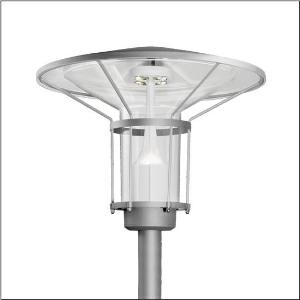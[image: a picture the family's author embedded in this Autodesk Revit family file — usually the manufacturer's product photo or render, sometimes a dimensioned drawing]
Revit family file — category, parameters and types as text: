
# Revit family: laterne_classic_iq___st1_2a_5xa5245af14h_9f1a
name_source: partatom
category: Lighting Fixtures
units: mm (PartAtom-declared; Revit-internal decimal feet)

## family parameters
Cut with Voids When Loaded = No
Host = Face
Light Source = No
Part Type = Normal
Room Calculation Point = No
Round Connector Dimension = Use Diameter
Shared = No

## types (1)
- --- (1 x LED, 1380 lm, 12.9 W, 2200K)
    Apparent Load = 13 VA
    CIE Flux Codes = 21 60 93 97 100
    Color Rendering = 70
    Color Temperature = 2200K
    Default Elevation = 1800 mm
    Description = Lantern Classic iQ, mast luminaire, Module 540 iQ-SR, primary light control with 3 zone facetted reflector, of plastic, silver coated, highly specular, structured, primary optical cover: cover, of PMMA, transparent, light distribution: ST1.2a, light emission: direct distribution, primary light characteristic: asymmetric, installation type: post-top, LED, High Power LED, rated luminous flux: 1.380lm, luminous efficacy: 107lm/W, light colour: 722, colour temperature: 2200K, control gear: ECG iQ, control: presetting dimming logarithmic, Street-Remote, Auto-Match, Temp-Guard, Lumen-Switch, Night-Set, Smart-Wire, Light-Fading, Desk-Remote (wireless, voltage-free reading and setting of iQ features in the workshop via application-optimized NFC function/RFID function), optimised constant luminous flux control (CLO 2.0), with terminal, 6-pole, max. 2.5mm², mains connection: 230..240V, AC, 50/60Hz, start of lifetime: 13W, end of service life: 13W, reduction: 6W, luminaire housing, upper part, of glass-fibre reinforced polyester, coated, Siteco® metallic grey (DB 702S), diameter: 750mm, height: 596mm, spigot size: d x l = 76 x 70mm (post-top) | with reducer (optional accessory) 60 x 70mm, post-top mast mounting element, of diecast aluminium, coated, Siteco® metallic grey (DB 702S), Module 540 iQ-SR, traffic white (RAL 9016), equipment: standard, protection rating (complete): IP65, insulation class (complete): insulation class II (safety insulation), certification: CE, ENEC, VDE, packaging unit: 1 piece

Light Distribution: ST1.2a
    Height = 596 mm
    Lamp = 1 x LED
    Lamp Light Flux = 1380 lm
    Lamp Power = 12.9 W
    Lamp count = 1
    Length = 750 mm
    Luminous efficacy = 107 lm/W
    Manufacturer = Siteco
    ModVariant = No
    Model = 5XA5245AF14H
    Number of Poles = 1
    OnlyDefault = Yes
    Power Factor = 1
    Product Name = Laterne Classic iQ | ST1.2a
    Product group = mast luminaire | pylon top
    ProductGroupID = 6100
    Protection Class = Protection class II
    Protection Degree = IP 65
    RLX_Detail_Level = 1
    RLX_Emergency_Light_Flux = 0 lm
    RLX_Emergency_Type = 0
    RLX_Emergency_Type_DB = No
    RlxData = <blob elided: 92033 chars, md5=dd218689>
    Socket = socket
    Standby Power = 0 W
    System Light Flux = 1380 lm
    System Power = 13 W
    Type Comments = factory setting: luminous flux: 100 % | dim-lin: 254 | 516 mA
    Type Image = l_1006052.jpg
    URL = http://relux.com
    VarID = @adj_110583
    Voltage = 0 V
    Weight = 0.00 kg
    Width = 0 mm  [stored 0 ft]

note: [stored X ft] marks values corroborated as IEEE doubles in the binary element streams (Revit-internal decimal feet)

## geometry (parser evidence)
native form markers: Blend x4, Sweep x12
no freeform markers — native parametric forms only
